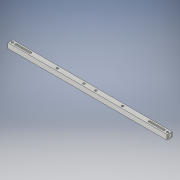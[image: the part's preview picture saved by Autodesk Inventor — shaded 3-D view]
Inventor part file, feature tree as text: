
AUTODESK INVENTOR PART (.ipt)
format: ipt  version: 2019 (Build 230136000, 136)  size: 146,432 bytes
history: native  units: mm
features: extrude x2, sketch x2, mirror x1
ambient origin geometry x8: Origin, YZ Plane, XZ Plane, XY Plane, X Axis, Y Axis, Z Axis, Center Point
bodies: Solid1 (feature_tree)
feature tree (5):
  extrude  "Extrusion1"  Depth=12.7mm
  extrude  "Extrusion2"  Depth=5.2mm
  mirror  "Mirror1"
  sketch  "Sketch1"  dims[d0=12.7mm d1=12.7mm]
  sketch  "Sketch2"  dims[d4=400.0mm d5=0.0mm d6=5.2mm d7=5.0mm d8=9.0mm d9=36.0mm d10=100.0mm d11=0.0mm d13=67.0mm d14=15.0mm d15=2.0mm d16=2.0mm]
